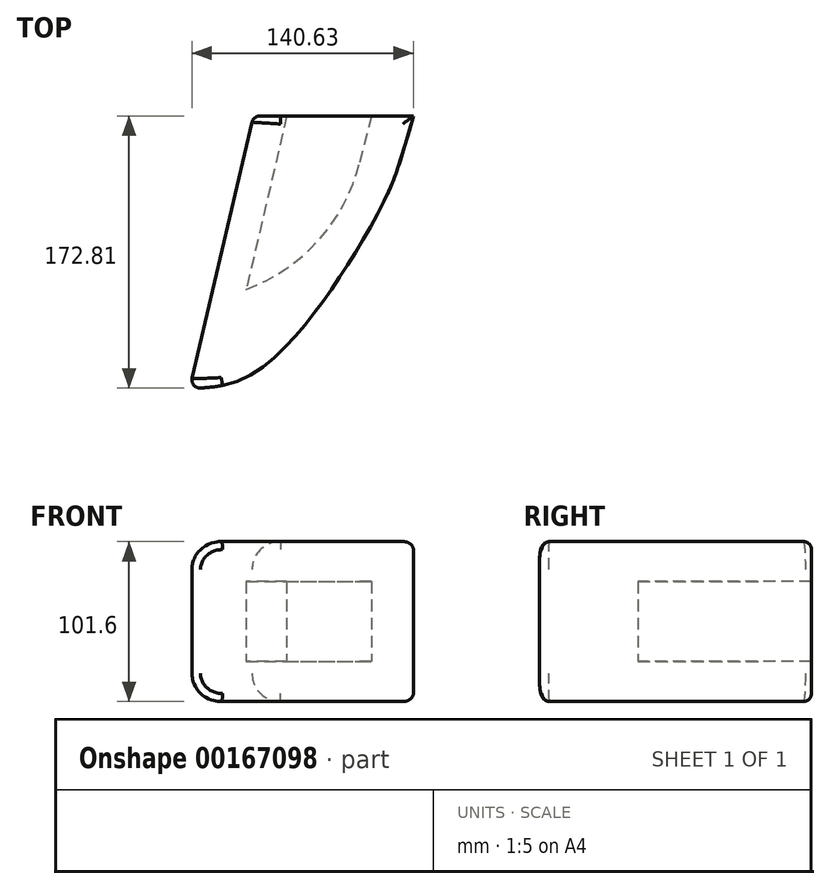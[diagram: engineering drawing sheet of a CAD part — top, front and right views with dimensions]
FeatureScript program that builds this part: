
annotation { "Feature Type Name" : "Feature", "Feature Type Description" : "" }
export const myFeature = defineFeature(function(context is Context, id is Id, definition is map)
    precondition{}
    {
        {
            var Q0;
            Q0=qCreatedBy(makeId("Top.planeOp"),FACE);
            var sketch = newSketch(context, id + "F0", { "sketchPlane" : qUnion([Q0])});
            skLineSegment(sketch, "E0", {"start": v(-51.34, 7.31) * mm, "end": v(2.46, 7.31) * mm});
            skLineSegment(sketch, "E1", {"start": v(-51.34, 7.31) * mm, "end": v(-77.34, -104.03) * mm});
            skLineSegment(sketch, "E2", {"start": v(2.46, 7.31) * mm, "end": v(-5.34, -23.71) * mm});
            skArc(sketch, "E3", {"start": v(-77.34, -104.03) * mm, "mid": v(-31.42, -72.76) * mm, "end": v(-5.34, -23.71) * mm});
            skSolve(sketch);
        }
        {
            var Q0;
            Q0=qCreatedBy(makeId("Top.planeOp"),FACE);
            var sketch = newSketch(context, id + "F1", { "sketchPlane" : qUnion([Q0])});
            skLineSegment(sketch, "E4", {"start": v(-72.78, 6.15) * mm, "end": v(28.82, 6.15) * mm});
            skLineSegment(sketch, "E5", {"start": v(-72.78, 6.15) * mm, "end": v(-113.21, -167) * mm});
            skFitSpline(sketch, "E6", {"points": [v(28.82, 6.15) * mm, v(17.76, -30.18) * mm, v(4.9, -58.13) * mm, v(-30.87, -114.57) * mm, v(-77.26, -159.85) * mm, v(-113.21, -167) * mm], "startDerivative": vector(-59.57, -212.34) * mm, "endDerivative": vector(-201.59, -9.13) * mm});
            skSolve(sketch);
        }
        {
            var Q0;
            Q0=qSketchRegion(id+"F1",true);
            extrude(context, id + "F2", {"entities" : qUnion([Q0]), "endBound" : BoundingType.SYMMETRIC, "offsetDistance" : 25.4 * mm, "depth" : 101.6 * mm});
        }
        {
            var Q0;
            Q0=makeQuery(id+"F2.opExtrude","CAP_EDGE",EDGE,{"disambiguationData":[OSD([sQuery(id+"F1.wireOp",EDGE,"C4H4PHbU-KKx9-q2EA-dDIi-FWc9RiPhfjej")])],"isStart":false});
            var Q1;
            Q1=makeQuery(id+"F2.opExtrude","CAP_EDGE",EDGE,{"disambiguationData":[OSD([sQuery(id+"F1.wireOp",EDGE,"AuzyW1eY-Z02w-8Qvh-idDG-ZBL9Gl5PuICG")])],"isStart":false});
            var Q2;
            Q2=makeQuery(id+"F2.opExtrude","CAP_EDGE",EDGE,{"disambiguationData":[OSD([sQuery(id+"F1.wireOp",EDGE,"E5")])],"isStart":false});
            fillet(context, id + "F3", {"entities" : qUnion([Q0, Q1, Q2]), "radius" : 17.78 * mm, "tangentPropagation" : true, "allowEdgeOverflow" : false});
        }
        {
            var Q0;
            Q0=makeQuery(id+"F2.opExtrude","CAP_EDGE",EDGE,{"disambiguationData":[OSD([sQuery(id+"F1.wireOp",EDGE,"AuzyW1eY-Z02w-8Qvh-idDG-ZBL9Gl5PuICG")])],"isStart":true});
            var Q1;
            Q1=makeQuery(id+"F2.opExtrude","CAP_EDGE",EDGE,{"disambiguationData":[OSD([sQuery(id+"F1.wireOp",EDGE,"C4H4PHbU-KKx9-q2EA-dDIi-FWc9RiPhfjej")])],"isStart":true});
            var Q2;
            Q2=makeQuery(id+"F2.opExtrude","CAP_EDGE",EDGE,{"disambiguationData":[OSD([sQuery(id+"F1.wireOp",EDGE,"E5")])],"isStart":true});
            fillet(context, id + "F4", {"entities" : qUnion([Q0, Q1, Q2]), "radius" : 17.78 * mm, "tangentPropagation" : true, "allowEdgeOverflow" : false});
        }
        {
            var Q0;
            Q0 = qSketchRegion(id + "F0", true);
            extrude(context, id + "F5", {"entities" : qUnion([Q0]), "operationType" : NewBodyOperationType.REMOVE, "endBound" : BoundingType.SYMMETRIC, "depth" : 50.8 * mm, "offsetDistance" : 25.4 * mm});
        }
        {
            var Q0;
            Q0=makeQuery(id+"F2.opExtrude","CAP_FACE",FACE,{"disambiguationData":[OSD([sQuery(id+"F1.wireOp",EDGE,"E4"),sQuery(id+"F1.wireOp",EDGE,"E5"),sQuery(id+"F1.wireOp",EDGE,"E6")])],"isStart":false});
            fillet(context, id + "F6", {"entities" : qUnion([Q0]), "radius" : 5.08 * mm, "tangentPropagation" : true, "allowEdgeOverflow" : false});
        }
    });
